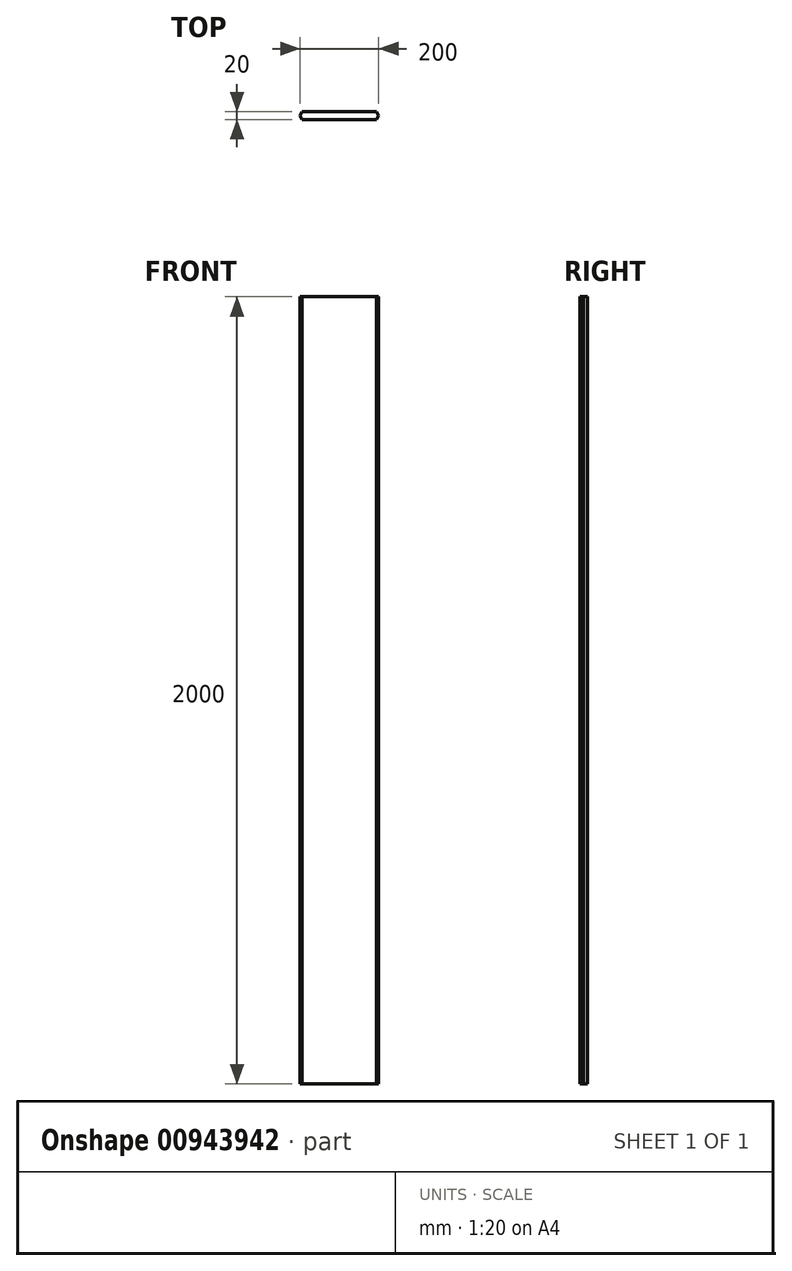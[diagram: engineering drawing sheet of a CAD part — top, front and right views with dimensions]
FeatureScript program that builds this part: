
annotation { "Feature Type Name" : "Feature", "Feature Type Description" : "" }
export const myFeature = defineFeature(function(context is Context, id is Id, definition is map)
    precondition{}
    {
        {
            var Q0;
            Q0=qCreatedBy(makeId("Top.planeOp"),FACE);
            var sketch = newSketch(context, id + "F0", { "sketchPlane" : qUnion([Q0])});
            skLineSegment(sketch, "E0", {"start": v(-100, 0) * mm, "end": v(-94.23, 10) * mm});
            skLineSegment(sketch, "E1", {"start": v(-94.23, 10) * mm, "end": v(94.23, 10) * mm});
            skLineSegment(sketch, "E2", {"start": v(94.23, 10) * mm, "end": v(100, 0) * mm});
            skLineSegment(sketch, "E3", {"start": v(100, 0) * mm, "end": v(94.23, -10) * mm});
            skLineSegment(sketch, "E4", {"start": v(94.23, -10) * mm, "end": v(-94.23, -10) * mm});
            skLineSegment(sketch, "E5", {"start": v(-94.23, -10) * mm, "end": v(-100, 0) * mm});
            skSolve(sketch);
        }
        {
            var Q0;
            Q0 = qSketchRegion(id + "F0", true);
            extrude(context, id + "F1", {"entities" : qUnion([Q0]), "depth" : 2000 * mm, "offsetDistance" : 25 * mm});
        }
    });
